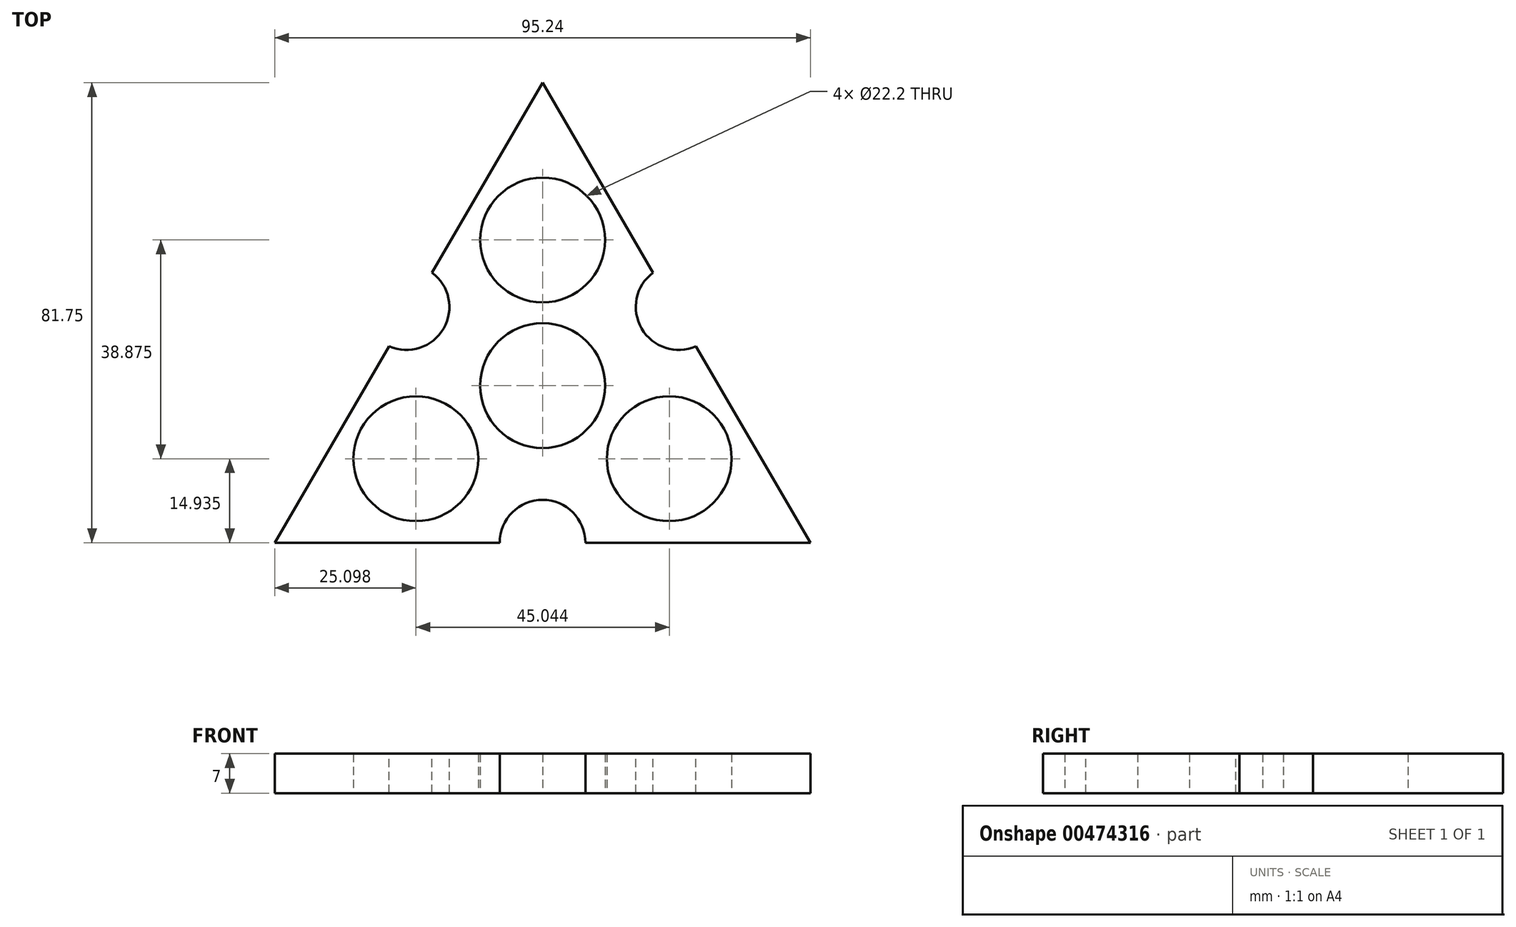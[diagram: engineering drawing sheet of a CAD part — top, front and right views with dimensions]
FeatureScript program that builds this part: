
annotation { "Feature Type Name" : "Feature", "Feature Type Description" : "" }
export const myFeature = defineFeature(function(context is Context, id is Id, definition is map)
    precondition{}
    {
        {
            var Q0;
            Q0=qCreatedBy(makeId("Top.planeOp"),FACE);
            var sketch = newSketch(context, id + "F0", { "sketchPlane" : qUnion([Q0])});
            skCircle(sketch, "E0", {"center": v(0, 0) * mm, "radius": 11.1 * mm});
            skCircle(sketch, "E1", {"center": v(0, 25.87) * mm, "radius": 11.1 * mm});
            skCircle(sketch, "E2.1.1", {"center": v(-22.52, -13) * mm, "radius": 11.1 * mm});
            skCircle(sketch, "E2.2.1", {"center": v(22.52, -13) * mm, "radius": 11.1 * mm});
            skPoint(sketch, "E2.center", {"position": v(-2.86, -6.61) * mm});
            skPoint(sketch, "E3.trimOffspring.end.orphan", {"position": v(15.24, 0) * mm});
            skPoint(sketch, "E4.orphan", {"position": v(-7.62, 13.2) * mm});
            skPoint(sketch, "E5.orphan", {"position": v(-15.24, 0) * mm});
            skPoint(sketch, "E6.orphan", {"position": v(15.24, 40.64) * mm});
            skPoint(sketch, "E7.trimOffspring.end.orphan", {"position": v(0, 40.64) * mm});
            skPoint(sketch, "E8.left.end.orphan", {"position": v(-15.24, 40.64) * mm});
            skPoint(sketch, "E9.start.orphan", {"position": v(0, 11.1) * mm});
            skLineSegment(sketch, "E10", {"start": v(-47.62, -27.94) * mm, "end": v(47.63, -27.94) * mm});
            skLineSegment(sketch, "E11", {"start": v(0, 0) * mm, "end": v(0, -37.56) * mm});
            skLineSegment(sketch, "E12", {"start": v(-47.63, -27.94) * mm, "end": v(0, 53.81) * mm});
            skLineSegment(sketch, "E13", {"start": v(0, 53.81) * mm, "end": v(47.63, -27.94) * mm});
            skSolve(sketch);
        }
        {
            var Q0;
            Q0 = qSketchRegion(id + "F0", true);
            extrude(context, id + "F1", {"entities" : qUnion([Q0]), "depth" : 7 * mm});
        }
        {
            var Q0;
            Q0=makeQuery(id+"F1.opExtrude","CAP_FACE",FACE,{"disambiguationData":[OSD([sQuery(id+"F0.wireOp",EDGE,"E0"),sQuery(id+"F0.wireOp",EDGE,"E1"),sQuery(id+"F0.wireOp",EDGE,"E2.1.1"),sQuery(id+"F0.wireOp",EDGE,"E2.2.1"),sQuery(id+"F0.wireOp",EDGE,"E10"),sQuery(id+"F0.wireOp",EDGE,"E12"),sQuery(id+"F0.wireOp",EDGE,"E13")])],"isStart":false});
            var sketch = newSketch(context, id + "F2", { "sketchPlane" : qUnion([Q0])});
            skCircle(sketch, "E14", {"center": v(0, -27.94) * mm, "radius": 7.62 * mm});
            skCircle(sketch, "E15.1.0", {"center": v(24.2, 13.97) * mm, "radius": 7.62 * mm});
            skCircle(sketch, "E15.2.0", {"center": v(-24.2, 13.97) * mm, "radius": 7.62 * mm});
            skPoint(sketch, "E15.center", {"position": v(0, 0) * mm});
            skSolve(sketch);
        }
        {
            var Q0;
            Q0 = qSketchRegion(id + "F2", true);
            extrude(context, id + "F3", {"entities" : qUnion([Q0]), "operationType" : NewBodyOperationType.REMOVE, "oppositeDirection" : true, "depth" : 25.4 * mm});
        }
    });
